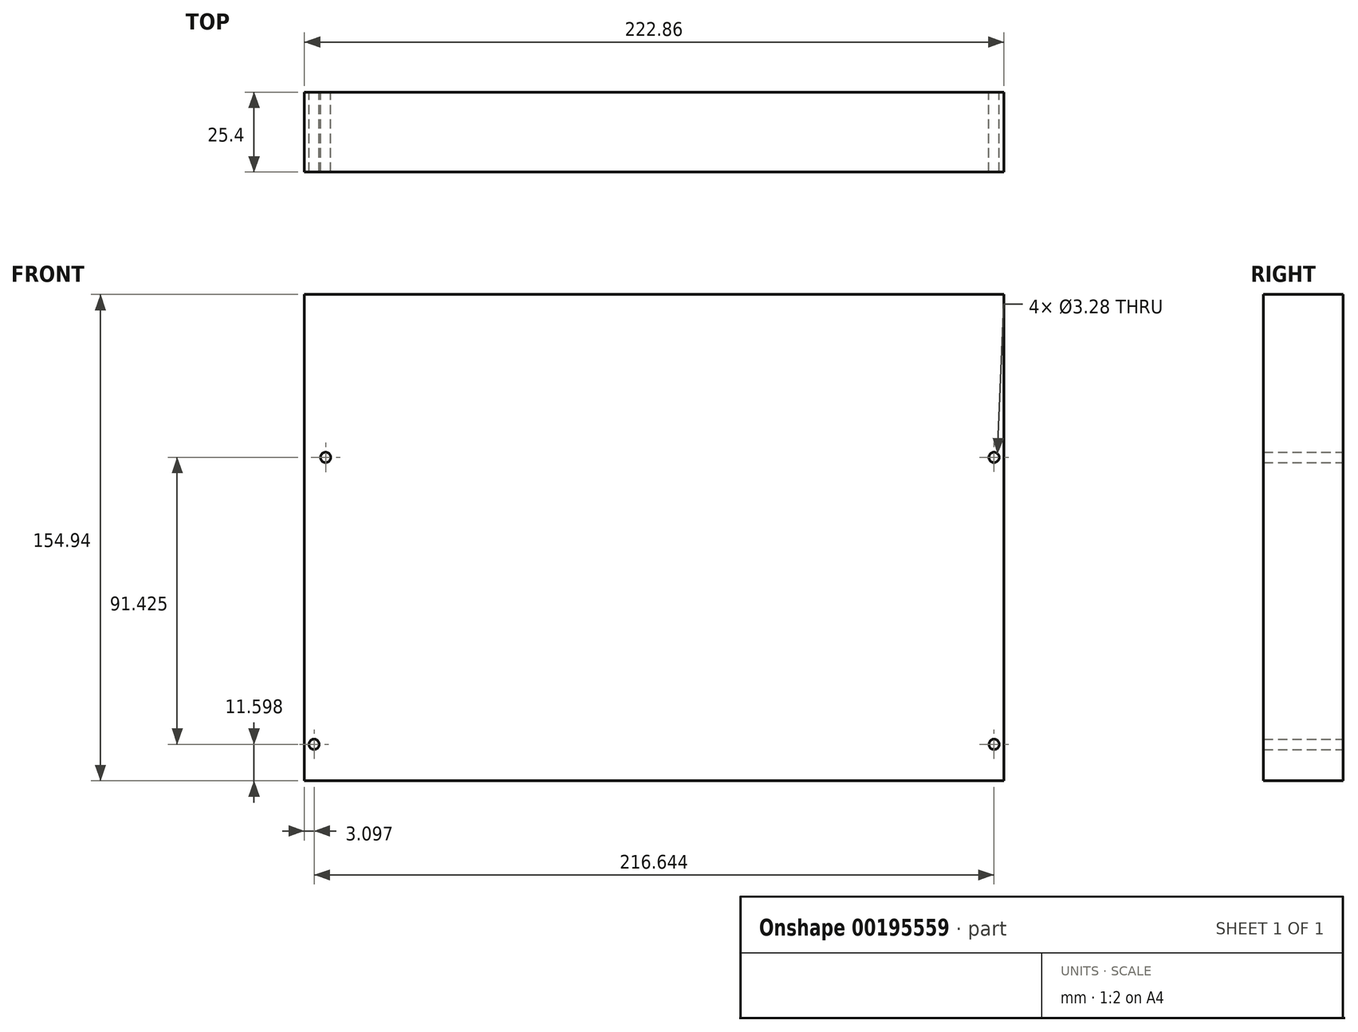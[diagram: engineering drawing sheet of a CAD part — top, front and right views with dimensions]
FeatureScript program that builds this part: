
annotation { "Feature Type Name" : "Feature", "Feature Type Description" : "" }
export const myFeature = defineFeature(function(context is Context, id is Id, definition is map)
    precondition{}
    {
        {
            var Q0;
            Q0=qCreatedBy(makeId("Front.planeOp"),FACE);
            var sketch = newSketch(context, id + "F0", { "sketchPlane" : qUnion([Q0])});
            skLineSegment(sketch, "E0", {"start": v(-77.6, 0) * mm, "end": v(145.26, 0) * mm});
            skLineSegment(sketch, "E1", {"start": v(-77.6, 0) * mm, "end": v(-77.6, 154.94) * mm});
            skLineSegment(sketch, "E2", {"start": v(145.26, 0) * mm, "end": v(145.26, 154.94) * mm});
            skLineSegment(sketch, "E3", {"start": v(145.26, 154.94) * mm, "end": v(-77.6, 154.94) * mm});
            skCircle(sketch, "E4", {"center": v(-74.5, 11.6) * mm, "radius": 1.64 * mm});
            skCircle(sketch, "E5", {"center": v(-70.82, 103.02) * mm, "radius": 1.64 * mm});
            skCircle(sketch, "E6", {"center": v(142.14, 11.6) * mm, "radius": 1.64 * mm});
            skCircle(sketch, "E7", {"center": v(-160.62, 126.78) * mm, "radius": 1.64 * mm});
            skCircle(sketch, "E8", {"center": v(142.13, 103.02) * mm, "radius": 1.64 * mm});
            skLineSegment(sketch, "E9", {"start": v(-77.6, 11.6) * mm, "end": v(-76.14, 11.6) * mm});
            skSolve(sketch);
        }
        {
            var Q0;
            {var subQ3=sQuery(id+"F0.wireOp",EDGE,"E0");Q0=makeQuery(id+"F0.imprint","IMPRINT",FACE,{"disambiguationData":[TD([[makeQuery(id+"F0.imprint","IMPRINT",EDGE,{"derivedFrom":subQ3}),1.0]])]});}
            extrude(context, id + "F1", {"entities" : qUnion([Q0]), "depth" : 25.4 * mm});
        }
    });
